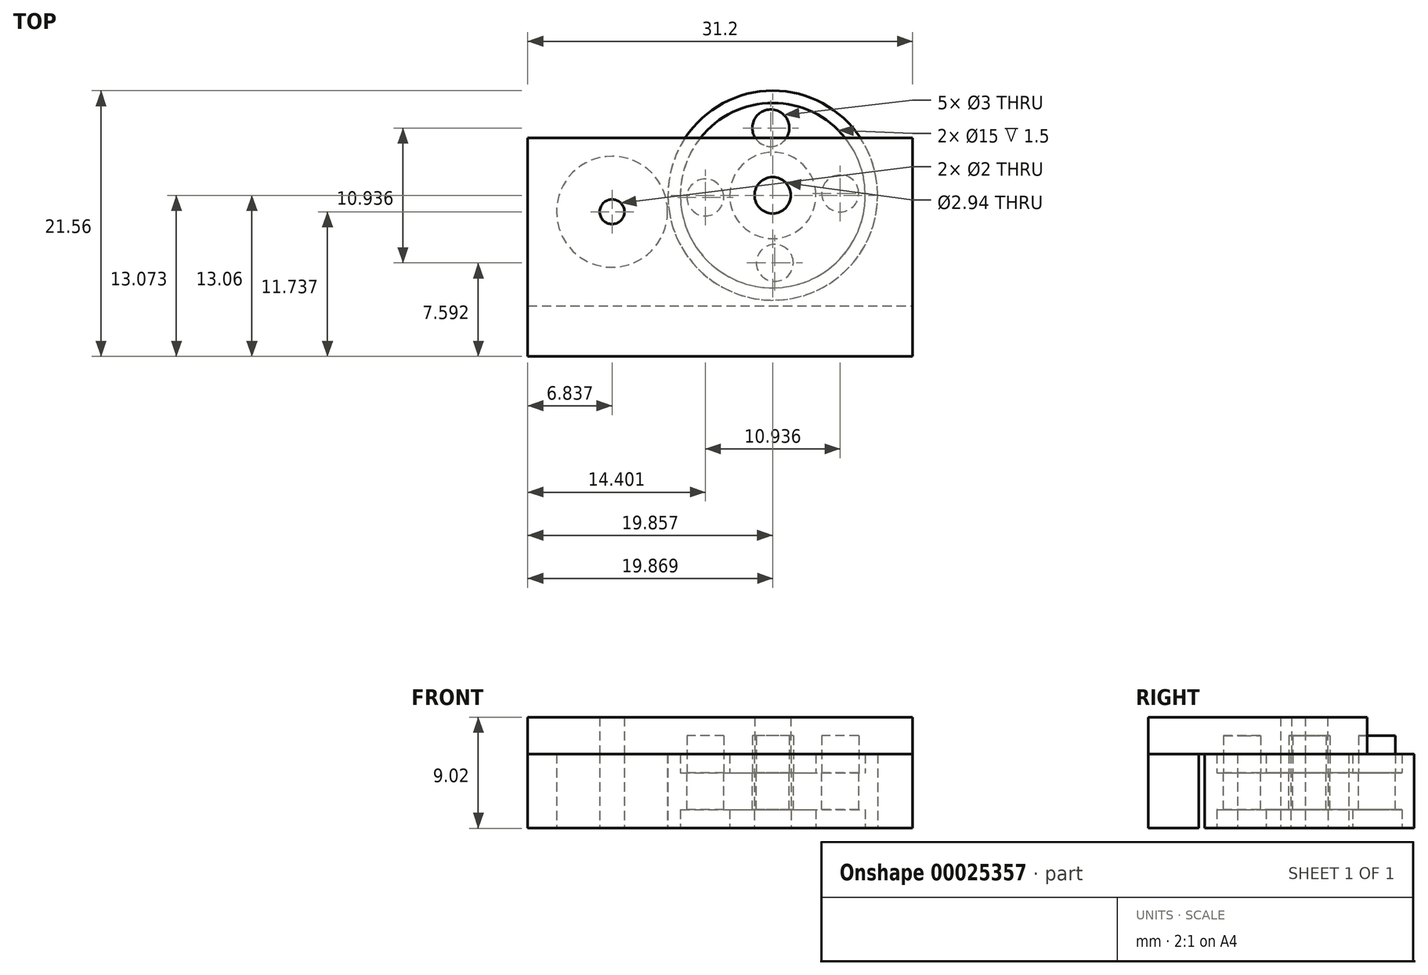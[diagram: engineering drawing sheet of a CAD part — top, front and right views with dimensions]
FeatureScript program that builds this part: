
annotation { "Feature Type Name" : "Feature", "Feature Type Description" : "" }
export const myFeature = defineFeature(function(context is Context, id is Id, definition is map)
    precondition{}
    {
        {
            var Q0;
            Q0=qCreatedBy(makeId("Top.planeOp"),FACE);
            var sketch = newSketch(context, id + "F0", { "sketchPlane" : qUnion([Q0])});
            skCircle(sketch, "E0", {"center": v(0.56, -1.32) * mm, "radius": 1 * mm});
            skCircle(sketch, "E1", {"center": v(0.56, -1.32) * mm, "radius": 4.5 * mm});
            skLineSegment(sketch, "E2.bottom", {"start": v(1.42, 3.1) * mm, "end": v(-0.08, 3.1) * mm});
            skSolve(sketch);
        }
        {
            var Q0;
            Q0 = qSketchRegion(id + "F0", true);
            var Q1;
            Q1=sQuery(id+"F0.wireOp",EDGE,"E0");
            var Q2;
            Q2=sQuery(id+"F0.wireOp",EDGE,"E1");
            var Q3;
            Q3=sQuery(id+"F0.wireOp",EDGE,"E2.bottom");
            extrude(context, id + "F1", {"entities" : qUnion([Q0]), "surfaceEntities" : qUnion([Q1, Q2, Q3]), "depth" : 6 * mm});
        }
        {
            var Q0;
            Q0=qCreatedBy(makeId("Front.planeOp"),FACE);
            var sketch = newSketch(context, id + "F2", { "sketchPlane" : qUnion([Q0])});
            skLineSegment(sketch, "E3.right", {"start": v(5.09, -0.02) * mm, "end": v(5.09, 5.98) * mm});
            skLineSegment(sketch, "E4.bottom", {"start": v(10.09, 5.98) * mm, "end": v(6.09, 5.98) * mm});
            skLineSegment(sketch, "E4.top", {"start": v(10.09, 4.48) * mm, "end": v(6.09, 4.48) * mm});
            skLineSegment(sketch, "E5.bottom", {"start": v(6.09, -0.02) * mm, "end": v(10.09, -0.02) * mm});
            skLineSegment(sketch, "E5.top", {"start": v(6.09, 1.48) * mm, "end": v(10.09, 1.48) * mm});
            skLineSegment(sketch, "E3.bottom", {"start": v(12.09, -0.02) * mm, "end": v(5.09, -0.02) * mm});
            skLineSegment(sketch, "E3.top", {"start": v(12.09, 5.98) * mm, "end": v(5.09, 5.98) * mm});
            skLineSegment(sketch, "E3.left", {"start": v(12.09, -0.02) * mm, "end": v(12.09, 5.98) * mm});
            skLineSegment(sketch, "E6", {"start": v(13.59, 5.55) * mm, "end": v(13.59, 10.08) * mm, "construction": true});
            skLineSegment(sketch, "E4.left", {"start": v(10.09, 5.98) * mm, "end": v(10.09, 4.48) * mm});
            skLineSegment(sketch, "E4.right", {"start": v(6.09, 5.98) * mm, "end": v(6.09, 4.48) * mm});
            skLineSegment(sketch, "E5.left", {"start": v(6.09, -0.02) * mm, "end": v(6.09, 1.48) * mm});
            skLineSegment(sketch, "E5.right", {"start": v(10.09, -0.02) * mm, "end": v(10.09, 1.48) * mm});
            skLineSegment(sketch, "E7", {"start": v(13.59, 4) * mm, "end": v(13.59, 5.55) * mm, "construction": true});
            skSolve(sketch);
        }
        {
            var Q0;
            {var subQ6=sQuery(id+"F2.wireOp",EDGE,"E3.right");Q0=makeQuery(id+"F2.imprint","IMPRINT",FACE,{"disambiguationData":[TD([[makeQuery(id+"F2.imprint","IMPRINT",EDGE,{"derivedFrom":subQ6}),-1.0]])]});}
            var Q1;
            Q1=sQuery(id+"F2.wireOp",EDGE,"E3.right");
            var Q2;
            Q2=sQuery(id+"F2.wireOp",EDGE,"E4.bottom");
            var Q3;
            Q3=sQuery(id+"F2.wireOp",EDGE,"E4.top");
            var Q4;
            Q4=sQuery(id+"F2.wireOp",EDGE,"E5.bottom");
            var Q5;
            Q5=sQuery(id+"F2.wireOp",EDGE,"E5.top");
            var Q6;
            Q6=sQuery(id+"F2.wireOp",EDGE,"E3.bottom");
            var Q7;
            Q7=sQuery(id+"F2.wireOp",EDGE,"E3.top");
            var Q8;
            Q8=sQuery(id+"F2.wireOp",EDGE,"E4.left");
            var Q9;
            Q9=sQuery(id+"F2.wireOp",EDGE,"E4.right");
            var Q10;
            Q10=sQuery(id+"F2.wireOp",EDGE,"E5.left");
            var Q11;
            Q11=sQuery(id+"F2.wireOp",EDGE,"E5.right");
            var Q12;
            Q12=sQuery(id+"F2.wireOp",EDGE,"E6");
            revolve(context, id + "F3", {"entities" : qUnion([Q0]), "surfaceEntities" : qUnion([Q1, Q2, Q3, Q4, Q5, Q6, Q7, Q8, Q9, Q10, Q11]), "axis" : qUnion([Q12]), "revolveType" : RevolveType.FULL});
        }
        {
            var Q0;
            Q0=makeQuery(id+"F3.opRevolve","SWEPT_FACE",FACE,{"disambiguationData":[OSD([sQuery(id+"F2.wireOp",EDGE,"E4.top")])]});
            var sketch = newSketch(context, id + "F4", { "sketchPlane" : qUnion([Q0])});
            skCircle(sketch, "E8", {"center": v(13.43, 5.47) * mm, "radius": 1.5 * mm});
            skCircle(sketch, "E9.1.0", {"center": v(8.12, -0.16) * mm, "radius": 1.5 * mm});
            skCircle(sketch, "E9.2.0", {"center": v(13.75, -5.47) * mm, "radius": 1.5 * mm});
            skPoint(sketch, "E9.center", {"position": v(13.59, 0) * mm});
            skCircle(sketch, "E10.1.3.0", {"center": v(19.06, 0.16) * mm, "radius": 1.5 * mm});
            skSolve(sketch);
        }
        {
            var Q0;
            Q0 = qSketchRegion(id + "F4", true);
            extrude(context, id + "F5", {"entities" : qUnion([Q0]), "operationType" : NewBodyOperationType.REMOVE, "endBound" : BoundingType.THROUGH_ALL, "oppositeDirection" : true, "depth" : 25 * mm});
        }
        {
            var Q0;
            Q0=makeQuery(id+"F1.opExtrude","CAP_FACE",FACE,{"disambiguationData":[OSD([sQuery(id+"F0.wireOp",EDGE,"E0"),sQuery(id+"F0.wireOp",EDGE,"E1")])],"isStart":false});
            var sketch = newSketch(context, id + "F6", { "sketchPlane" : qUnion([Q0])});
            skLineSegment(sketch, "E11.bottom", {"start": v(-6.28, 4.67) * mm, "end": v(24.92, 4.67) * mm});
            skLineSegment(sketch, "E11.top", {"start": v(-6.28, -13.06) * mm, "end": v(24.92, -13.06) * mm});
            skLineSegment(sketch, "E11.left", {"start": v(-6.28, 4.67) * mm, "end": v(-6.28, -13.06) * mm});
            skLineSegment(sketch, "E11.right", {"start": v(24.92, 4.67) * mm, "end": v(24.92, -13.06) * mm});
            skCircle(sketch, "E12", {"center": v(0.56, -1.32) * mm, "radius": 1 * mm});
            skPoint(sketch, "E12.first.point", {"position": v(0.78, -0.35) * mm});
            skPoint(sketch, "E12.second.point", {"position": v(1.4, -1.86) * mm});
            skPoint(sketch, "E12.third.point", {"position": v(-0.35, -1.74) * mm});
            skCircle(sketch, "E13", {"center": v(13.58, 0.01) * mm, "radius": 1.47 * mm});
            skPoint(sketch, "E13.first.point", {"position": v(13.87, 1.45) * mm});
            skPoint(sketch, "E13.second.point", {"position": v(14.93, -0.57) * mm});
            skPoint(sketch, "E13.third.point", {"position": v(12.82, -1.25) * mm});
            skSolve(sketch);
        }
        {
            var Q0;
            Q0 = qSketchRegion(id + "F6", true);
            var Q1;
            Q1 = qSketchRegion(id + "F4", true);
            extrude(context, id + "F7", {"entities" : qUnion([Q0, Q1]), "depth" : 3 * mm});
        }
        {
            var Q0;
            Q0=makeQuery(id+"F7.opExtrude","CAP_FACE",FACE,{"disambiguationData":[OSD([sQuery(id+"F6.wireOp",EDGE,"E11.bottom"),sQuery(id+"F6.wireOp",EDGE,"E11.top"),sQuery(id+"F6.wireOp",EDGE,"E11.left"),sQuery(id+"F6.wireOp",EDGE,"E11.right"),sQuery(id+"F6.wireOp",EDGE,"E12"),sQuery(id+"F6.wireOp",EDGE,"E13")])],"isStart":true});
            var sketch = newSketch(context, id + "F8", { "sketchPlane" : qUnion([Q0])});
            skLineSegment(sketch, "E14.bottom", {"start": v(-6.28, 13.06) * mm, "end": v(24.92, 13.06) * mm});
            skLineSegment(sketch, "E14.top", {"start": v(-6.28, 8.96) * mm, "end": v(24.92, 8.96) * mm});
            skLineSegment(sketch, "E14.left", {"start": v(-6.28, 13.06) * mm, "end": v(-6.28, 8.96) * mm});
            skLineSegment(sketch, "E14.right", {"start": v(24.92, 13.06) * mm, "end": v(24.92, 8.96) * mm});
            skSolve(sketch);
        }
        {
            var Q0;
            Q0 = qSketchRegion(id + "F8", true);
            extrude(context, id + "F9", {"entities" : qUnion([Q0]), "depth" : 6 * mm});
        }
    });
